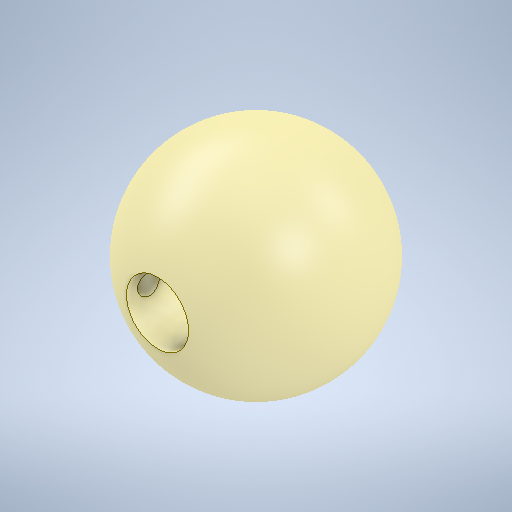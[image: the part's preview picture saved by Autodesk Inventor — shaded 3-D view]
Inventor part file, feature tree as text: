
AUTODESK INVENTOR PART (.ipt)
format: ipt  version: 2025.2 (Build 292293000, 293)  size: 437,760 bytes
history: native  units: mm
features: other x3, sketch x3, extrude x1
ambient origin geometry x8: Origin, YZ Plane, XZ Plane, XY Plane, X Axis, Y Axis, Z Axis, Center Point
bodies: Body1 (feature_tree)
feature tree (7):
  other  "Sólido1"
  other  "Revolução1"
  other  "Revolução2"
  extrude  "Extrusão1"  Depth=3.0mm
  sketch  "Esboço1"  dims[d0=10.0mm d2=3.0mm]
  sketch  "Esboço2"  dims[d3=360.0deg]
  sketch  "Esboço4"  dims[d4=1.0mm d5=4.0mm d6=10.0mm d7=360.0deg d10=3.0mm d11=10.0mm d12=0.0mm]
